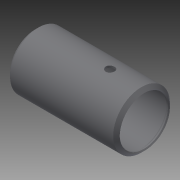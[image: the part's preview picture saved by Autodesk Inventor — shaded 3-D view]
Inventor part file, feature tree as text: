
AUTODESK INVENTOR PART (.ipt)
format: ipt  version: 2014 (Build 180170000, 170)  size: 144,384 bytes
history: native  units: in
note: dims shown in document units (in); Inventor stores cm internally (conversion verified against a paired STEP export)
features: other x56, revolve x2, sketch x2
ambient origin geometry x8: Origin, YZ Plane, XZ Plane, XY Plane, X Axis, Y Axis, Z Axis, Center Point
bodies: Solid1 (feature_tree)
feature tree (60):
  revolve  "Revolution1"  Angle=360.0deg
  revolve  "Revolution2"  [1 undecoded]
  other  "o1_XY"
  other  "o1_YZ"
  other  "o1_ZX"
  other  "o1_X"
  other  "o1_Y"
  other  "o1_Z"
  other  "o1_Center"
  other  "o2_XY"
  other  "o2_YZ"
  other  "o2_ZX"
  other  "o2_X"
  other  "o2_Y"
  other  "o2_Z"
  other  "o2_Center"
  other  "t1_XY"
  other  "t1_YZ"
  other  "t1_ZX"
  other  "t1_X"
  other  "t1_Y"
  other  "t1_Z"
  other  "t1_Center"
  other  "t2_XY"
  other  "t2_YZ"
  other  "t2_ZX"
  other  "t2_X"
  other  "t2_Y"
  other  "t2_Z"
  other  "t2_Center"
  other  "t3_XY"
  other  "t3_YZ"
  other  "t3_ZX"
  other  "t3_X"
  other  "t3_Y"
  other  "t3_Z"
  other  "t3_Center"
  other  "t4_XY"
  other  "t4_YZ"
  other  "t4_ZX"
  other  "t4_X"
  other  "t4_Y"
  other  "t4_Z"
  other  "t4_Center"
  other  "tube1_XY"
  other  "tube1_YZ"
  other  "tube1_ZX"
  other  "tube1_X"
  other  "tube1_Y"
  other  "tube1_Z"
  other  "tube1_Center"
  other  "tube2_XY"
  other  "tube2_YZ"
  other  "tube2_ZX"
  other  "tube2_X"
  other  "tube2_Y"
  other  "tube2_Z"
  other  "tube2_Center"
  sketch  "Sketch_5"
  sketch  "Sketch_1"  dims[d0=360.0deg d1=360.0deg]
note: 1 required parameter value undecoded (feature->parameter linkage not recoverable at this tier; creation-order binding heuristic only, values carry confidence <= 0.55)
